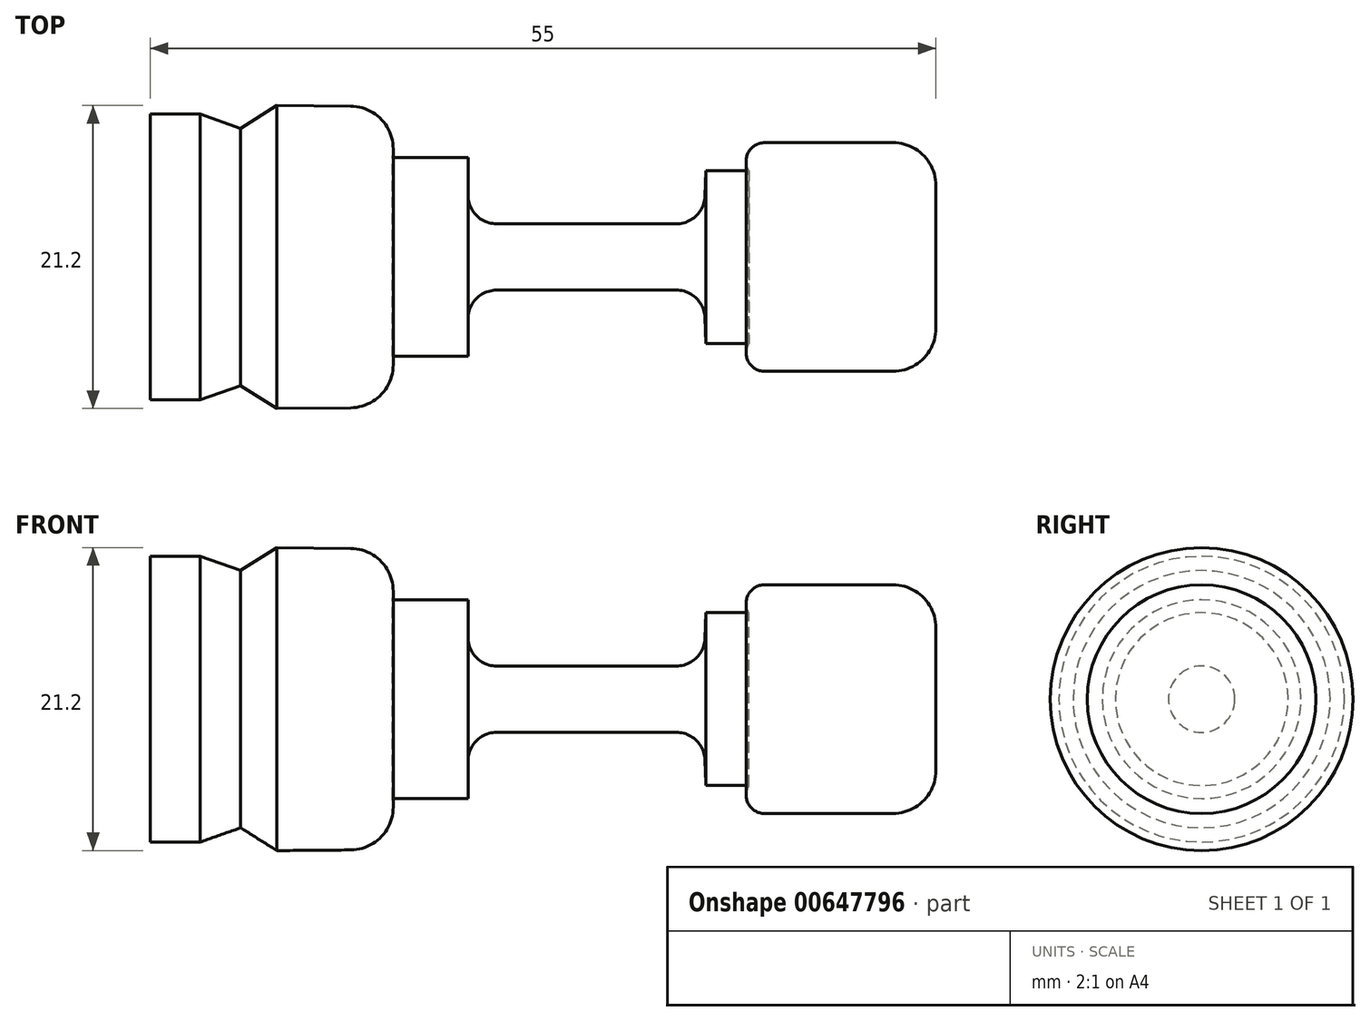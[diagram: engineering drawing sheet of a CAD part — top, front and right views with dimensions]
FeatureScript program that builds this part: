
annotation { "Feature Type Name" : "Feature", "Feature Type Description" : "" }
export const myFeature = defineFeature(function(context is Context, id is Id, definition is map)
    precondition{}
    {
        {
            var Q0;
            Q0=qCreatedBy(makeId("Front.planeOp"),FACE);
            var sketch = newSketch(context, id + "F0", { "sketchPlane" : qUnion([Q0])});
            skLineSegment(sketch, "E0", {"start": v(-36.65, 27.7) * mm, "end": v(18.35, 27.7) * mm});
            skLineSegment(sketch, "E1", {"start": v(-36.65, 27.7) * mm, "end": v(-36.65, 17.7) * mm});
            skLineSegment(sketch, "E2", {"start": v(-36.65, 17.7) * mm, "end": v(-33.15, 17.7) * mm});
            skLineSegment(sketch, "E3", {"start": v(-33.15, 17.7) * mm, "end": v(-30.33, 18.7) * mm});
            skLineSegment(sketch, "E4", {"start": v(-30.33, 18.7) * mm, "end": v(-27.79, 17.1) * mm});
            skLineSegment(sketch, "E5", {"start": v(18.35, 27.7) * mm, "end": v(18.35, 22.7) * mm});
            skLineSegment(sketch, "E6", {"start": v(15.35, 19.7) * mm, "end": v(6.35, 19.7) * mm});
            skLineSegment(sketch, "E7", {"start": v(0.18, 25.38) * mm, "end": v(-12.4, 25.38) * mm});
            skLineSegment(sketch, "E8", {"start": v(-14.4, 23.38) * mm, "end": v(-14.4, 20.74) * mm});
            skLineSegment(sketch, "E9", {"start": v(-14.4, 20.74) * mm, "end": v(-19.7, 20.74) * mm});
            skLineSegment(sketch, "E10", {"start": v(-22.62, 17.15) * mm, "end": v(-27.79, 17.1) * mm});
            skPoint(sketch, "E11.visualSharp", {"position": v(18.35, 19.7) * mm});
            skArc(sketch, "E11.filletArc", {"start": v(15.35, 19.7) * mm, "mid": v(17.47, 20.58) * mm, "end": v(18.35, 22.7) * mm});
            skArc(sketch, "E12.filletArc", {"start": v(5.25, 21.65) * mm, "mid": v(5.23, 20.36) * mm, "end": v(6.35, 19.7) * mm});
            skPoint(sketch, "E13.visualSharp", {"position": v(2.53, 25.38) * mm});
            skPoint(sketch, "E14.visualSharp", {"position": v(-14.4, 25.38) * mm});
            skArc(sketch, "E14.filletArc", {"start": v(-12.4, 25.38) * mm, "mid": v(-13.82, 24.8) * mm, "end": v(-14.4, 23.38) * mm});
            skPoint(sketch, "E15.visualSharp", {"position": v(-19.69, 17.17) * mm});
            skArc(sketch, "E15.filletArc", {"start": v(-22.62, 17.15) * mm, "mid": v(-20.31, 18.26) * mm, "end": v(-19.7, 20.74) * mm});
            skLineSegment(sketch, "E16", {"start": v(5.25, 21.65) * mm, "end": v(2.25, 21.65) * mm});
            skLineSegment(sketch, "E17", {"start": v(2.18, 23.47) * mm, "end": v(2.25, 21.65) * mm});
            skPoint(sketch, "E18.visualSharp", {"position": v(2.1, 25.38) * mm});
            skArc(sketch, "E18.filletArc", {"start": v(2.18, 23.47) * mm, "mid": v(1.56, 24.82) * mm, "end": v(0.18, 25.38) * mm});
            skLineSegment(sketch, "E19", {"start": v(-36.65, 27.7) * mm, "end": v(-47.86, 27.7) * mm, "construction": true});
            skSolve(sketch);
        }
        {
            var Q0;
            Q0=qSketchRegion(id+"F0",true);
            var Q1;
            Q1=sQuery(id+"F0.wireOp",EDGE,"E19");
            revolve(context, id + "F1", {"entities" : qUnion([Q0]), "axis" : qUnion([Q1]), "revolveType" : RevolveType.FULL});
        }
    });
